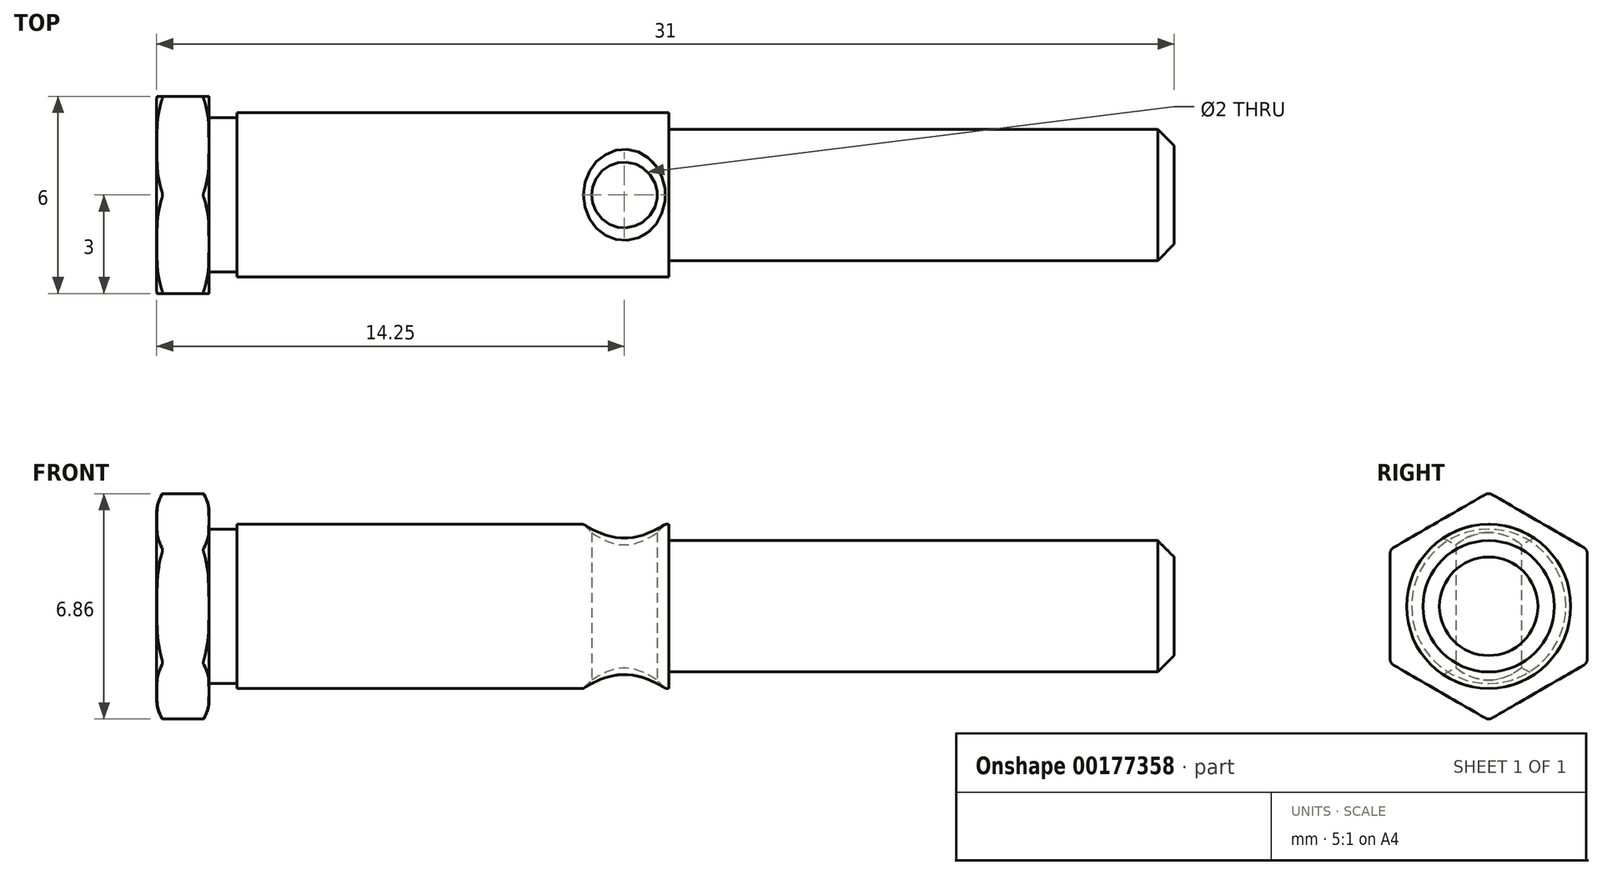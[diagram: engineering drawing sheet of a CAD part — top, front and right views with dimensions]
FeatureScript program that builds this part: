
annotation { "Feature Type Name" : "Feature", "Feature Type Description" : "" }
export const myFeature = defineFeature(function(context is Context, id is Id, definition is map)
    precondition{}
    {
        {
            var Q0;
            Q0=qCreatedBy(makeId("Front.planeOp"),FACE);
            var sketch = newSketch(context, id + "F0", { "sketchPlane" : qUnion([Q0])});
            skLineSegment(sketch, "E0", {"start": v(2.45, 2.5) * mm, "end": v(15.6, 2.5) * mm});
            skLineSegment(sketch, "E1", {"start": v(15.6, 2) * mm, "end": v(31, 2) * mm});
            skLineSegment(sketch, "E2", {"start": v(31, 2) * mm, "end": v(31, 0) * mm});
            skLineSegment(sketch, "E3", {"start": v(31, 0) * mm, "end": v(0, 0) * mm});
            skLineSegment(sketch, "E4", {"start": v(0, 2.35) * mm, "end": v(2.45, 2.35) * mm});
            skLineSegment(sketch, "E5", {"start": v(2.45, 2.35) * mm, "end": v(2.45, 2.5) * mm});
            skLineSegment(sketch, "E6", {"start": v(0, 2.35) * mm, "end": v(0, 0) * mm});
            skLineSegment(sketch, "E7", {"start": v(15.6, 2.5) * mm, "end": v(15.6, 2) * mm});
            skSolve(sketch);
        }
        {
            var Q0;
            Q0 = qSketchRegion(id + "F0", true);
            var Q1;
            Q1=sQuery(id+"F0.wireOp",EDGE,"E3");
            revolve(context, id + "F1", {"surfaceOperationType" : NewSurfaceOperationType.NEW, "entities" : qUnion([Q0]), "axis" : qUnion([Q1]), "revolveType" : RevolveType.FULL});
        }
        {
            var Q0;
            Q0=makeQuery(id+"F1.opRevolve","SWEPT_EDGE",EDGE,{"disambiguationData":[OSD([sQuery(id+"F0.wireOp",EDGE,"E1"),sQuery(id+"F0.wireOp",EDGE,"E2")])]});
            chamfer(context, id + "F2", {"entities" : qUnion([Q0]), "width" : 0.5 * mm, "tangentPropagation" : true});
        }
        {
            var Q0;
            Q0=makeQuery(id+"F1.opRevolve","SWEPT_FACE",FACE,{"disambiguationData":[OSD([sQuery(id+"F0.wireOp",EDGE,"E6")])]});
            var sketch = newSketch(context, id + "F3", { "sketchPlane" : qUnion([Q0])});
            skCircle(sketch, "E8.cCircle", {"center": v(0, 0) * mm, "radius": 3 * mm, "construction": true});
            skLineSegment(sketch, "E8.0", {"start": v(3, 1.73) * mm, "end": v(3, -1.73) * mm});
            skLineSegment(sketch, "E8.1", {"start": v(3, -1.73) * mm, "end": v(0, -3.46) * mm});
            skLineSegment(sketch, "E8.2", {"start": v(0, -3.46) * mm, "end": v(-3, -1.73) * mm});
            skLineSegment(sketch, "E8.3", {"start": v(-3, -1.73) * mm, "end": v(-3, 1.73) * mm});
            skLineSegment(sketch, "E8.4", {"start": v(-3, 1.73) * mm, "end": v(0, 3.46) * mm});
            skLineSegment(sketch, "E8.5", {"start": v(0, 3.46) * mm, "end": v(3, 1.73) * mm});
            skPoint(sketch, "E8.0.midPoint", {"position": v(3, 0) * mm});
            skSolve(sketch);
        }
        {
            var Q0;
            Q0 = qSketchRegion(id + "F3", true);
            extrude(context, id + "F4", {"entities" : qUnion([Q0]), "operationType" : NewBodyOperationType.ADD, "oppositeDirection" : true, "depth" : 1.6 * mm, "offsetDistance" : 25 * mm});
        }
        {
            var Q0;
            Q0=qCreatedBy(makeId("Front.planeOp"),FACE);
            var sketch = newSketch(context, id + "F5", { "sketchPlane" : qUnion([Q0])});
            skArc(sketch, "E9", {"start": v(1.6, 2.86) * mm, "mid": v(1.54, 3.2) * mm, "end": v(1.38, 3.49) * mm});
            skArc(sketch, "E10", {"start": v(0.22, 3.49) * mm, "mid": v(0.06, 3.2) * mm, "end": v(0, 2.86) * mm});
            skLineSegment(sketch, "E11", {"start": v(0.22, 3.49) * mm, "end": v(-0.23, 3.73) * mm});
            skLineSegment(sketch, "E12", {"start": v(-0.23, 3.73) * mm, "end": v(0, 2.86) * mm});
            skLineSegment(sketch, "E13", {"start": v(1.38, 3.49) * mm, "end": v(1.94, 3.88) * mm});
            skLineSegment(sketch, "E14", {"start": v(1.94, 3.88) * mm, "end": v(1.6, 2.86) * mm});
            skLineSegment(sketch, "E15", {"start": v(0, 0) * mm, "end": v(1.82, 0) * mm, "construction": true});
            skSolve(sketch);
        }
        {
            var Q0;
            Q0 = qSketchRegion(id + "F5", true);
            var Q1;
            Q1=sQuery(id+"F5.wireOp",EDGE,"E15");
            revolve(context, id + "F6", {"operationType" : NewBodyOperationType.REMOVE, "surfaceOperationType" : NewSurfaceOperationType.NEW, "entities" : qUnion([Q0]), "axis" : qUnion([Q1]), "revolveType" : RevolveType.FULL, "oppositeDirection" : true});
        }
        {
            var Q0;
            Q0=qCreatedBy(makeId("Top.planeOp"),FACE);
            var sketch = newSketch(context, id + "F7", { "sketchPlane" : qUnion([Q0])});
            skCircle(sketch, "E16", {"center": v(14.25, 0) * mm, "radius": 1 * mm});
            skSolve(sketch);
        }
        {
            var Q0;
            Q0 = qSketchRegion(id + "F7", true);
            extrude(context, id + "F8", {"entities" : qUnion([Q0]), "operationType" : NewBodyOperationType.REMOVE, "depth" : 25 * mm, "offsetDistance" : 25 * mm, "symmetric" : true});
        }
        {
            var Q0;
            Q0=makeQuery(id+"F8.boolean.opBoolean","COPY",FACE,{"derivedFrom":makeQuery(id+"F8.opExtrude","SWEPT_FACE",FACE,{"disambiguationData":[OSD([sQuery(id+"F7.wireOp",EDGE,"E16")])]})});
            chamfer(context, id + "F9", {"entities" : qUnion([Q0]), "width" : 0.25 * mm, "tangentPropagation" : true});
        }
        {
            var Q0;
            Q0=makeQuery(id+"F4.opExtrude","SWEPT_EDGE",EDGE,{"disambiguationData":[OSD([sQuery(id+"F3.wireOp",EDGE,"E8.1"),sQuery(id+"F3.wireOp",EDGE,"E8.2")])]});
            var Q1;
            Q1=makeQuery(id+"F4.opExtrude","SWEPT_EDGE",EDGE,{"disambiguationData":[OSD([sQuery(id+"F3.wireOp",EDGE,"E8.0"),sQuery(id+"F3.wireOp",EDGE,"E8.1")])]});
            var Q2;
            Q2=makeQuery(id+"F4.opExtrude","SWEPT_EDGE",EDGE,{"disambiguationData":[OSD([sQuery(id+"F3.wireOp",EDGE,"E8.0"),sQuery(id+"F3.wireOp",EDGE,"E8.5")])]});
            var Q3;
            Q3=makeQuery(id+"F4.opExtrude","SWEPT_EDGE",EDGE,{"disambiguationData":[OSD([sQuery(id+"F3.wireOp",EDGE,"E8.4"),sQuery(id+"F3.wireOp",EDGE,"E8.5")])]});
            var Q4;
            Q4=makeQuery(id+"F4.opExtrude","SWEPT_EDGE",EDGE,{"disambiguationData":[OSD([sQuery(id+"F3.wireOp",EDGE,"E8.3"),sQuery(id+"F3.wireOp",EDGE,"E8.4")])]});
            var Q5;
            Q5=makeQuery(id+"F4.opExtrude","SWEPT_EDGE",EDGE,{"disambiguationData":[OSD([sQuery(id+"F3.wireOp",EDGE,"E8.2"),sQuery(id+"F3.wireOp",EDGE,"E8.3")])]});
            fillet(context, id + "F10", {"entities" : qUnion([Q0, Q1, Q2, Q3, Q4, Q5]), "radius" : 0.2 * mm, "tangentPropagation" : true, "allowEdgeOverflow" : false});
        }
    });
